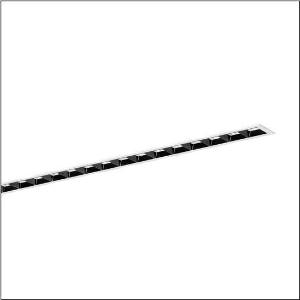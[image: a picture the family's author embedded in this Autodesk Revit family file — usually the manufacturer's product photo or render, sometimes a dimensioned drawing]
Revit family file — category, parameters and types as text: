
# Revit family: silica_r__21_51mx12da44wb_905f
name_source: partatom
category: Lighting Fixtures
units: mm (PartAtom-declared; Revit-internal decimal feet)

## family parameters
Cut with Voids When Loaded = No
Host = Face
Light Source = No
Part Type = Normal
Room Calculation Point = No
Round Connector Dimension = Use Diameter
Shared = No

## types (1)
- --- (1 x LED, 4320 lm, 25.6 W, 4000K)
    Apparent Load = 26 VA
    CIE Flux Codes = 86 100 100 100 100
    Color Rendering = 80
    Color Temperature = 4000K
    Default Elevation = 1800 mm
    Description = Silica® 21, office luminaire, primary light control with darklight reflector, of PMMA, black, CAT 2 (L<= 3000cd/m²), light emission: direct distribution, primary light characteristic: symmetric, installation type: recessed, LED, rated luminous flux: 4.320lm, luminous efficacy: 169lm/W, light colour: 840, colour temperature: 4000K, with terminal, 3+2-pole, max. 2.5mm², mains connection: 220..240V, AC, 50/60Hz, rated input power: 25.6W, luminaire housing, of aluminium, traffic white (RAL 9016), length: 1.228mm, width: 79mm, height: 53mm, protection rating (complete): IP20, insulation class (complete): insulation class I (protective earthing), certification: CE, permissible operating ambient temperature: 0..+35°C, standard: EN 50419, packaging unit: 1 piece
    Height = 0 mm  [stored 0 ft]
    Lamp = 1 x LED
    Lamp Light Flux = 4320 lm
    Lamp Power = 25.6 W
    Lamp count = 1
    Length = 1227 mm
    Luminous efficacy = 169 lm/W
    Manufacturer = Siteco
    ModVariant = No
    Model = 51MX12DA44WB
    Mounting Place = Ceiling
    Mounting Type = Recessed
    Number of Poles = 1
    OnlyDefault = Yes
    Power Factor = 1
    Product Name = Silica® 21
    Product group = office luminaire | ceiling recessed
    ProductGroupID = 401
    Protection Class = Protection class I
    Protection Degree = IP 20
    RLX_Detail_Level = 1
    RLX_Emergency_Light_Flux = 0 lm
    RLX_Emergency_Type = 0
    RLX_Emergency_Type_DB = No
    RlxData = <blob elided: 38617 chars, md5=b9b911b1>
    Socket = socket
    Standby Power = 0 W
    System Light Flux = 4320 lm
    System Power = 26 W
    Type Comments = factory setting: luminous flux: 100 % | dim-lin: 254 | 367 mA
    Type Image = l_1297791.jpg
    URL = http://relux.com
    VarID = @adj_055745
    Voltage = 0 V
    Weight = 0.00 kg
    Width = 79 mm

note: [stored X ft] marks values corroborated as IEEE doubles in the binary element streams (Revit-internal decimal feet)

## geometry (parser evidence)
native form markers: Blend x4, Sweep x11
no freeform markers — native parametric forms only
